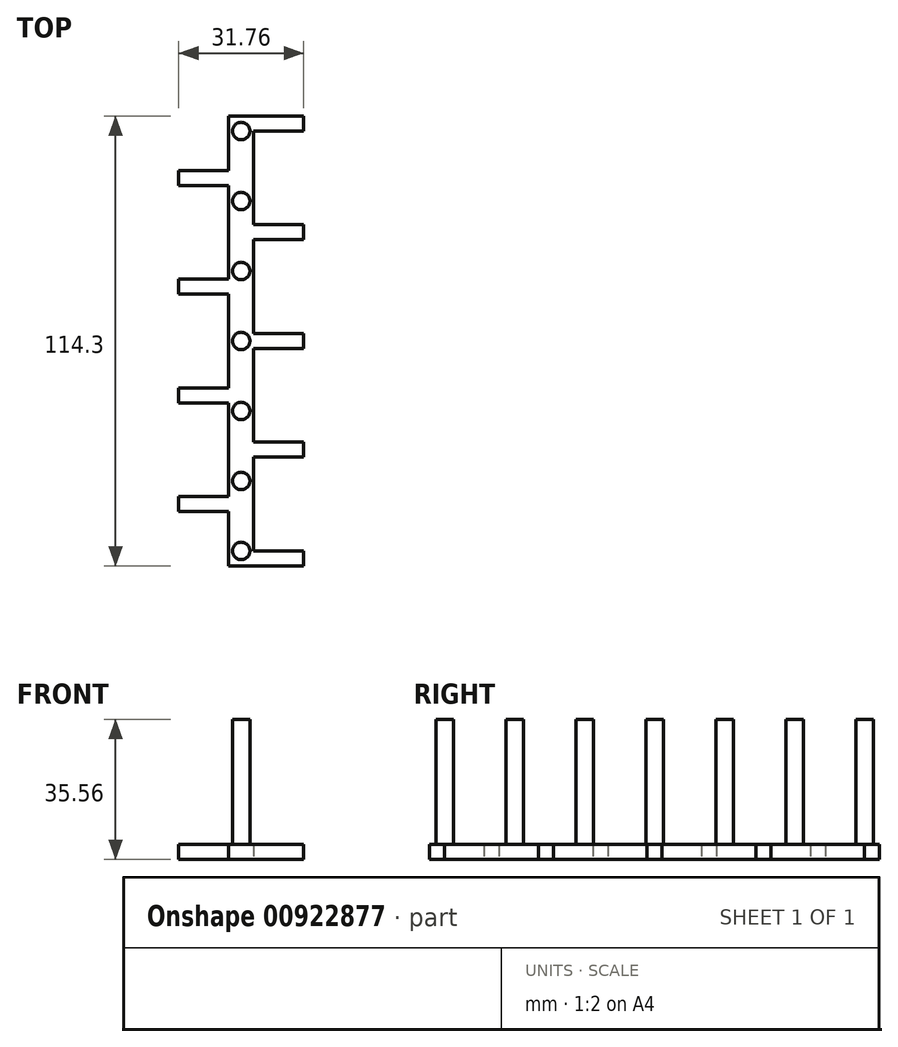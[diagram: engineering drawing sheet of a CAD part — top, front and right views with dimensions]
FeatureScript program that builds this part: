
annotation { "Feature Type Name" : "Feature", "Feature Type Description" : "" }
export const myFeature = defineFeature(function(context is Context, id is Id, definition is map)
    precondition{}
    {
        {
            var Q0;
            Q0=qCreatedBy(makeId("Top.planeOp"),FACE);
            var sketch = newSketch(context, id + "F0", { "sketchPlane" : qUnion([Q0])});
            skLineSegment(sketch, "E0.bottom", {"start": v(-3.18, 57.15) * mm, "end": v(3.17, 57.15) * mm});
            skLineSegment(sketch, "E0.top", {"start": v(-3.17, -57.15) * mm, "end": v(3.18, -57.15) * mm});
            skLineSegment(sketch, "E0.left", {"start": v(-3.18, 57.15) * mm, "end": v(-3.17, -57.15) * mm});
            skLineSegment(sketch, "E0.right", {"start": v(3.17, 57.15) * mm, "end": v(3.18, -57.15) * mm});
            skLineSegment(sketch, "E1.bottom", {"start": v(3.18, -57.15) * mm, "end": v(15.88, -57.15) * mm});
            skLineSegment(sketch, "E1.top", {"start": v(3.18, -53.34) * mm, "end": v(15.88, -53.34) * mm});
            skLineSegment(sketch, "E1.left", {"start": v(3.18, -57.15) * mm, "end": v(3.18, -53.34) * mm});
            skLineSegment(sketch, "E1.right", {"start": v(15.88, -57.15) * mm, "end": v(15.88, -53.34) * mm});
            skLineSegment(sketch, "E2.0.1.0", {"start": v(3.18, -25.72) * mm, "end": v(15.88, -25.72) * mm});
            skLineSegment(sketch, "E2.0.1.1", {"start": v(3.18, -29.53) * mm, "end": v(15.88, -29.53) * mm});
            skLineSegment(sketch, "E2.0.1.2", {"start": v(15.88, -29.53) * mm, "end": v(15.88, -25.72) * mm});
            skLineSegment(sketch, "E2.0.1.3", {"start": v(3.18, -29.53) * mm, "end": v(3.18, -25.72) * mm});
            skLineSegment(sketch, "E2.0.2.0", {"start": v(3.18, 1.9) * mm, "end": v(15.88, 1.9) * mm});
            skLineSegment(sketch, "E2.0.2.1", {"start": v(3.18, -1.9) * mm, "end": v(15.88, -1.9) * mm});
            skLineSegment(sketch, "E2.0.2.2", {"start": v(15.88, -1.9) * mm, "end": v(15.88, 1.9) * mm});
            skLineSegment(sketch, "E2.0.2.3", {"start": v(3.18, -1.9) * mm, "end": v(3.18, 1.9) * mm});
            skLineSegment(sketch, "E2.0.3.0", {"start": v(3.18, 29.53) * mm, "end": v(15.88, 29.53) * mm});
            skLineSegment(sketch, "E2.0.3.1", {"start": v(3.18, 25.72) * mm, "end": v(15.88, 25.72) * mm});
            skLineSegment(sketch, "E2.0.3.2", {"start": v(15.88, 25.72) * mm, "end": v(15.88, 29.53) * mm});
            skLineSegment(sketch, "E2.0.3.3", {"start": v(3.18, 25.72) * mm, "end": v(3.18, 29.53) * mm});
            skLineSegment(sketch, "E2.0.4.0", {"start": v(3.18, 57.15) * mm, "end": v(15.88, 57.15) * mm});
            skLineSegment(sketch, "E2.0.4.1", {"start": v(3.18, 53.34) * mm, "end": v(15.88, 53.34) * mm});
            skLineSegment(sketch, "E2.0.4.2", {"start": v(15.88, 53.34) * mm, "end": v(15.88, 57.15) * mm});
            skLineSegment(sketch, "E2.0.4.3", {"start": v(3.18, 53.34) * mm, "end": v(3.18, 57.15) * mm});
            skLineSegment(sketch, "E2.direction1", {"start": v(3.18, -53.34) * mm, "end": v(9.53, -53.34) * mm, "construction": true});
            skLineSegment(sketch, "E2.direction2", {"start": v(3.18, -53.34) * mm, "end": v(3.18, -25.72) * mm, "construction": true});
            skLineSegment(sketch, "E3.bottom", {"start": v(-3.17, -39.53) * mm, "end": v(-15.87, -39.53) * mm});
            skLineSegment(sketch, "E3.top", {"start": v(-3.17, -43.34) * mm, "end": v(-15.87, -43.34) * mm});
            skLineSegment(sketch, "E3.left", {"start": v(-3.17, -39.53) * mm, "end": v(-3.17, -43.34) * mm});
            skLineSegment(sketch, "E3.right", {"start": v(-15.87, -39.53) * mm, "end": v(-15.87, -43.34) * mm});
            skLineSegment(sketch, "E4.0.1.0", {"start": v(-15.87, -11.9) * mm, "end": v(-15.87, -15.72) * mm});
            skLineSegment(sketch, "E4.0.1.1", {"start": v(-3.17, -11.9) * mm, "end": v(-3.17, -15.72) * mm});
            skLineSegment(sketch, "E4.0.1.2", {"start": v(-3.17, -11.9) * mm, "end": v(-15.87, -11.9) * mm});
            skLineSegment(sketch, "E4.0.1.3", {"start": v(-3.17, -15.72) * mm, "end": v(-15.87, -15.72) * mm});
            skLineSegment(sketch, "E4.0.2.0", {"start": v(-15.87, 15.72) * mm, "end": v(-15.87, 11.9) * mm});
            skLineSegment(sketch, "E4.0.2.1", {"start": v(-3.17, 15.72) * mm, "end": v(-3.17, 11.9) * mm});
            skLineSegment(sketch, "E4.0.2.2", {"start": v(-3.17, 15.72) * mm, "end": v(-15.87, 15.72) * mm});
            skLineSegment(sketch, "E4.0.2.3", {"start": v(-3.17, 11.9) * mm, "end": v(-15.87, 11.9) * mm});
            skLineSegment(sketch, "E4.0.3.0", {"start": v(-15.87, 43.34) * mm, "end": v(-15.87, 39.53) * mm});
            skLineSegment(sketch, "E4.0.3.1", {"start": v(-3.17, 43.34) * mm, "end": v(-3.17, 39.53) * mm});
            skLineSegment(sketch, "E4.0.3.2", {"start": v(-3.17, 43.34) * mm, "end": v(-15.87, 43.34) * mm});
            skLineSegment(sketch, "E4.0.3.3", {"start": v(-3.17, 39.53) * mm, "end": v(-15.87, 39.53) * mm});
            skLineSegment(sketch, "E4.direction1", {"start": v(-9.52, -43.34) * mm, "end": v(-15.87, -43.34) * mm, "construction": true});
            skLineSegment(sketch, "E4.direction2", {"start": v(-15.87, -43.34) * mm, "end": v(-15.87, -15.72) * mm, "construction": true});
            skSolve(sketch);
        }
        {
            var Q0;
            {var subQ9=sQuery(id+"F0.wireOp",EDGE,"E2.0.1.0");var subQ17=sQuery(id+"F0.wireOp",EDGE,"E1.bottom");var subQ24=sQuery(id+"F0.wireOp",EDGE,"E2.0.3.0");var subQ32=sQuery(id+"F0.wireOp",EDGE,"E2.0.4.0");var subQ33=sQuery(id+"F0.wireOp",EDGE,"E0.bottom");var subQ37=sQuery(id+"F0.wireOp",EDGE,"E2.0.2.0");var subQ44=sQuery(id+"F0.wireOp",EDGE,"E3.bottom");Q0=qUnion([makeQuery(id+"F0.imprint","IMPRINT",FACE,{"disambiguationData":[TD([[makeQuery(id+"F0.imprint","IMPRINT",EDGE,{"derivedFrom":subQ33}),-1.0]])]}),makeQuery(id+"F0.imprint","IMPRINT",FACE,{"disambiguationData":[TD([[makeQuery(id+"F0.imprint","IMPRINT",EDGE,{"derivedFrom":subQ44}),1.0]])]}),makeQuery(id+"F0.imprint","IMPRINT",FACE,{"disambiguationData":[TD([[makeQuery(id+"F0.imprint","IMPRINT",EDGE,{"derivedFrom":subQ37}),-1.0]])]}),makeQuery(id+"F0.imprint","IMPRINT",FACE,{"disambiguationData":[TD([[makeQuery(id+"F0.imprint","IMPRINT",EDGE,{"derivedFrom":subQ32}),-1.0]])]}),makeQuery(id+"F0.imprint","IMPRINT",FACE,{"disambiguationData":[TD([[makeQuery(id+"F0.imprint","IMPRINT",EDGE,{"derivedFrom":sQuery(id+"F0.wireOp",EDGE,"E4.0.1.0")}),1.0]])]}),makeQuery(id+"F0.imprint","IMPRINT",FACE,{"disambiguationData":[TD([[makeQuery(id+"F0.imprint","IMPRINT",EDGE,{"derivedFrom":subQ24}),-1.0]])]}),makeQuery(id+"F0.imprint","IMPRINT",FACE,{"disambiguationData":[TD([[makeQuery(id+"F0.imprint","IMPRINT",EDGE,{"derivedFrom":subQ17}),1.0]])]}),makeQuery(id+"F0.imprint","IMPRINT",FACE,{"disambiguationData":[TD([[makeQuery(id+"F0.imprint","IMPRINT",EDGE,{"derivedFrom":sQuery(id+"F0.wireOp",EDGE,"E4.0.2.0")}),1.0]])]}),makeQuery(id+"F0.imprint","IMPRINT",FACE,{"disambiguationData":[TD([[makeQuery(id+"F0.imprint","IMPRINT",EDGE,{"derivedFrom":subQ9}),-1.0]])]}),makeQuery(id+"F0.imprint","IMPRINT",FACE,{"disambiguationData":[TD([[makeQuery(id+"F0.imprint","IMPRINT",EDGE,{"derivedFrom":sQuery(id+"F0.wireOp",EDGE,"E4.0.3.0")}),1.0]])]})]);}
            extrude(context, id + "F1", {"entities" : qUnion([Q0]), "depth" : 3.8 * mm, "offsetDistance" : 25.4 * mm});
        }
        {
            var Q0;
            Q0=makeQuery(id+"F1.opExtrude","CAP_FACE",FACE,{"disambiguationData":[OSD([sQuery(id+"F0.wireOp",EDGE,"E0.bottom"),sQuery(id+"F0.wireOp",EDGE,"E0.top"),sQuery(id+"F0.wireOp",EDGE,"E0.left"),sQuery(id+"F0.wireOp",EDGE,"E0.right"),sQuery(id+"F0.wireOp",EDGE,"E1.bottom"),sQuery(id+"F0.wireOp",EDGE,"E1.top"),sQuery(id+"F0.wireOp",EDGE,"E1.right"),sQuery(id+"F0.wireOp",EDGE,"E2.0.1.0"),sQuery(id+"F0.wireOp",EDGE,"E2.0.1.1"),sQuery(id+"F0.wireOp",EDGE,"E2.0.1.2"),sQuery(id+"F0.wireOp",EDGE,"E2.0.2.0"),sQuery(id+"F0.wireOp",EDGE,"E2.0.2.1"),sQuery(id+"F0.wireOp",EDGE,"E2.0.2.2"),sQuery(id+"F0.wireOp",EDGE,"E2.0.3.0"),sQuery(id+"F0.wireOp",EDGE,"E2.0.3.1"),sQuery(id+"F0.wireOp",EDGE,"E2.0.3.2"),sQuery(id+"F0.wireOp",EDGE,"E2.0.4.0"),sQuery(id+"F0.wireOp",EDGE,"E2.0.4.1"),sQuery(id+"F0.wireOp",EDGE,"E2.0.4.2"),sQuery(id+"F0.wireOp",EDGE,"E3.bottom"),sQuery(id+"F0.wireOp",EDGE,"E3.top"),sQuery(id+"F0.wireOp",EDGE,"E3.right"),sQuery(id+"F0.wireOp",EDGE,"E4.0.1.0"),sQuery(id+"F0.wireOp",EDGE,"E4.0.1.2"),sQuery(id+"F0.wireOp",EDGE,"E4.0.1.3"),sQuery(id+"F0.wireOp",EDGE,"E4.0.2.0"),sQuery(id+"F0.wireOp",EDGE,"E4.0.2.2"),sQuery(id+"F0.wireOp",EDGE,"E4.0.2.3"),sQuery(id+"F0.wireOp",EDGE,"E4.0.3.0"),sQuery(id+"F0.wireOp",EDGE,"E4.0.3.2"),sQuery(id+"F0.wireOp",EDGE,"E4.0.3.3")])],"isStart":false});
            var sketch = newSketch(context, id + "F2", { "sketchPlane" : qUnion([Q0])});
            skCircle(sketch, "E5", {"center": v(0, 0) * mm, "radius": 2.22 * mm});
            skCircle(sketch, "E6.0.1.0", {"center": v(0, 17.78) * mm, "radius": 2.22 * mm});
            skCircle(sketch, "E6.0.2.0", {"center": v(0, 35.56) * mm, "radius": 2.22 * mm});
            skCircle(sketch, "E6.0.3.0", {"center": v(0, 53.34) * mm, "radius": 2.22 * mm});
            skLineSegment(sketch, "E6.direction1", {"start": v(0, 0) * mm, "end": v(0, 0) * mm});
            skCircle(sketch, "E7.0.1.0", {"center": v(0, -17.78) * mm, "radius": 2.22 * mm});
            skCircle(sketch, "E7.0.2.0", {"center": v(0, -35.56) * mm, "radius": 2.22 * mm});
            skCircle(sketch, "E7.0.3.0", {"center": v(0, -53.34) * mm, "radius": 2.22 * mm});
            skSolve(sketch);
        }
        {
            var Q0;
            Q0 = qSketchRegion(id + "F2", true);
            extrude(context, id + "F3", {"entities" : qUnion([Q0]), "operationType" : NewBodyOperationType.ADD, "depth" : 31.75 * mm, "offsetDistance" : 25.4 * mm});
        }
    });
